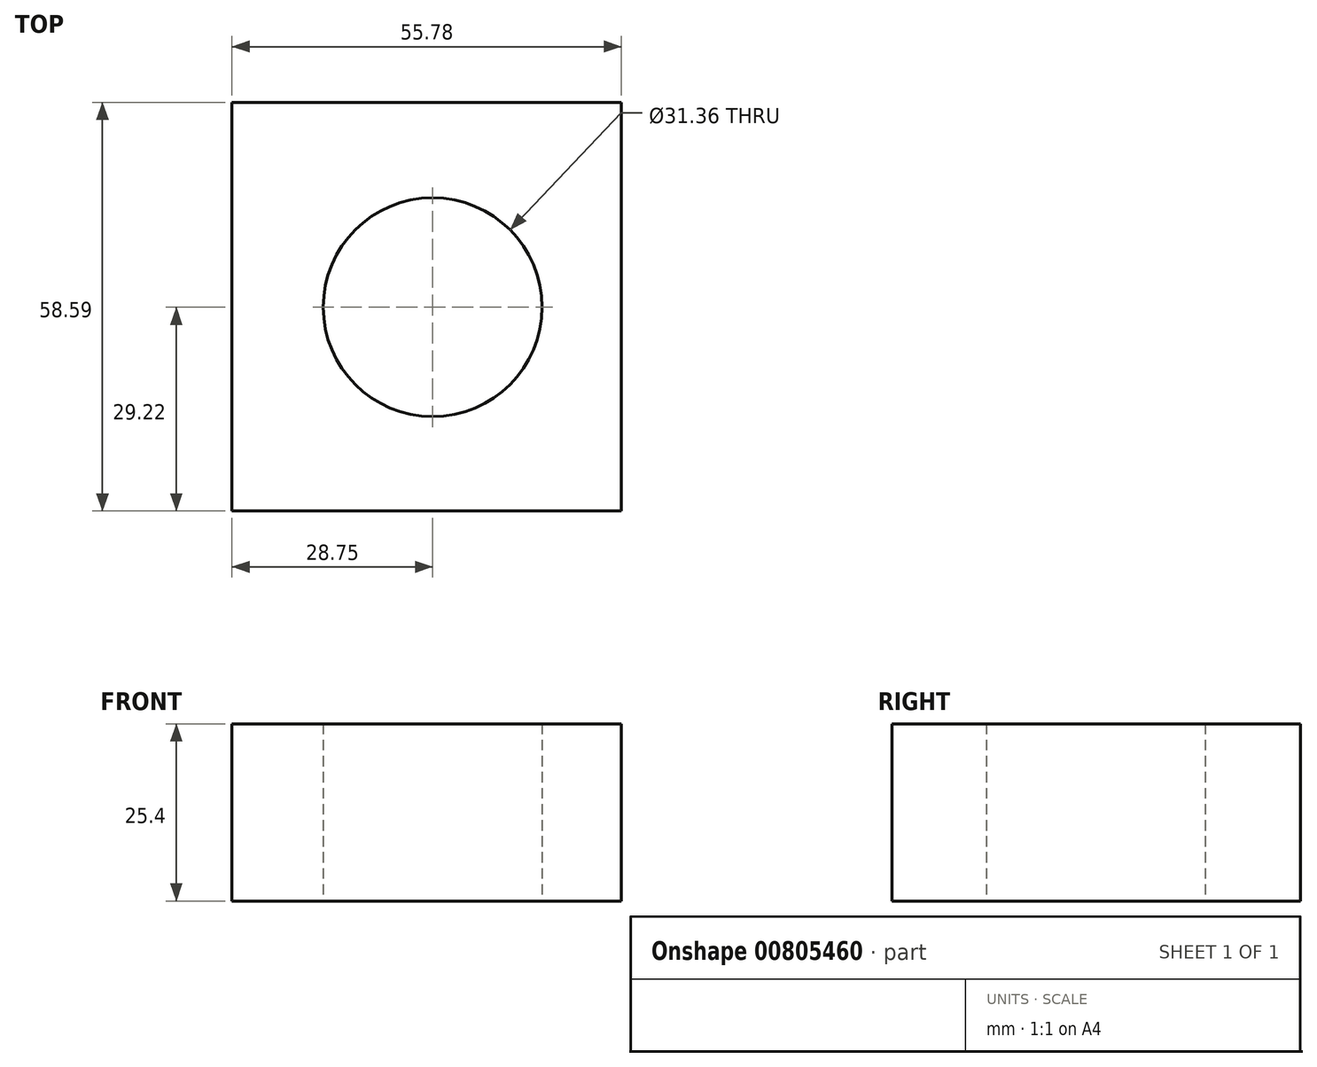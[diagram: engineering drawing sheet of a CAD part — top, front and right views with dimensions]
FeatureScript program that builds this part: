
annotation { "Feature Type Name" : "Feature", "Feature Type Description" : "" }
export const myFeature = defineFeature(function(context is Context, id is Id, definition is map)
    precondition{}
    {
        {
            var Q0;
            Q0=qCreatedBy(makeId("Top.planeOp"),FACE);
            var sketch = newSketch(context, id + "F0", { "sketchPlane" : qUnion([Q0])});
            skLineSegment(sketch, "E0.bottom", {"start": v(27.03, 29.37) * mm, "end": v(-28.75, 29.37) * mm});
            skLineSegment(sketch, "E0.top", {"start": v(27.03, -29.22) * mm, "end": v(-28.75, -29.22) * mm});
            skLineSegment(sketch, "E0.left", {"start": v(27.03, 29.37) * mm, "end": v(27.03, -29.22) * mm});
            skLineSegment(sketch, "E0.right", {"start": v(-28.75, 29.37) * mm, "end": v(-28.75, -29.22) * mm});
            skCircle(sketch, "E1", {"center": v(0, 0) * mm, "radius": 15.68 * mm});
            skSolve(sketch);
        }
        {
            var Q0;
            Q0=makeQuery(id+"F0.imprint","IMPRINT",FACE,{"disambiguationData":[TD([[makeQuery(id+"F0.imprint","IMPRINT",EDGE,{"derivedFrom":sQuery(id+"F0.wireOp",EDGE,"E0.bottom")}),1.0]])]});
            var Q1;
            Q1 = qSketchRegion(id + "F2", true);
            extrude(context, id + "F1", {"entities" : qUnion([Q0, Q1]), "depth" : 25.4 * mm, "offsetDistance" : 25.4 * mm});
        }
    });
